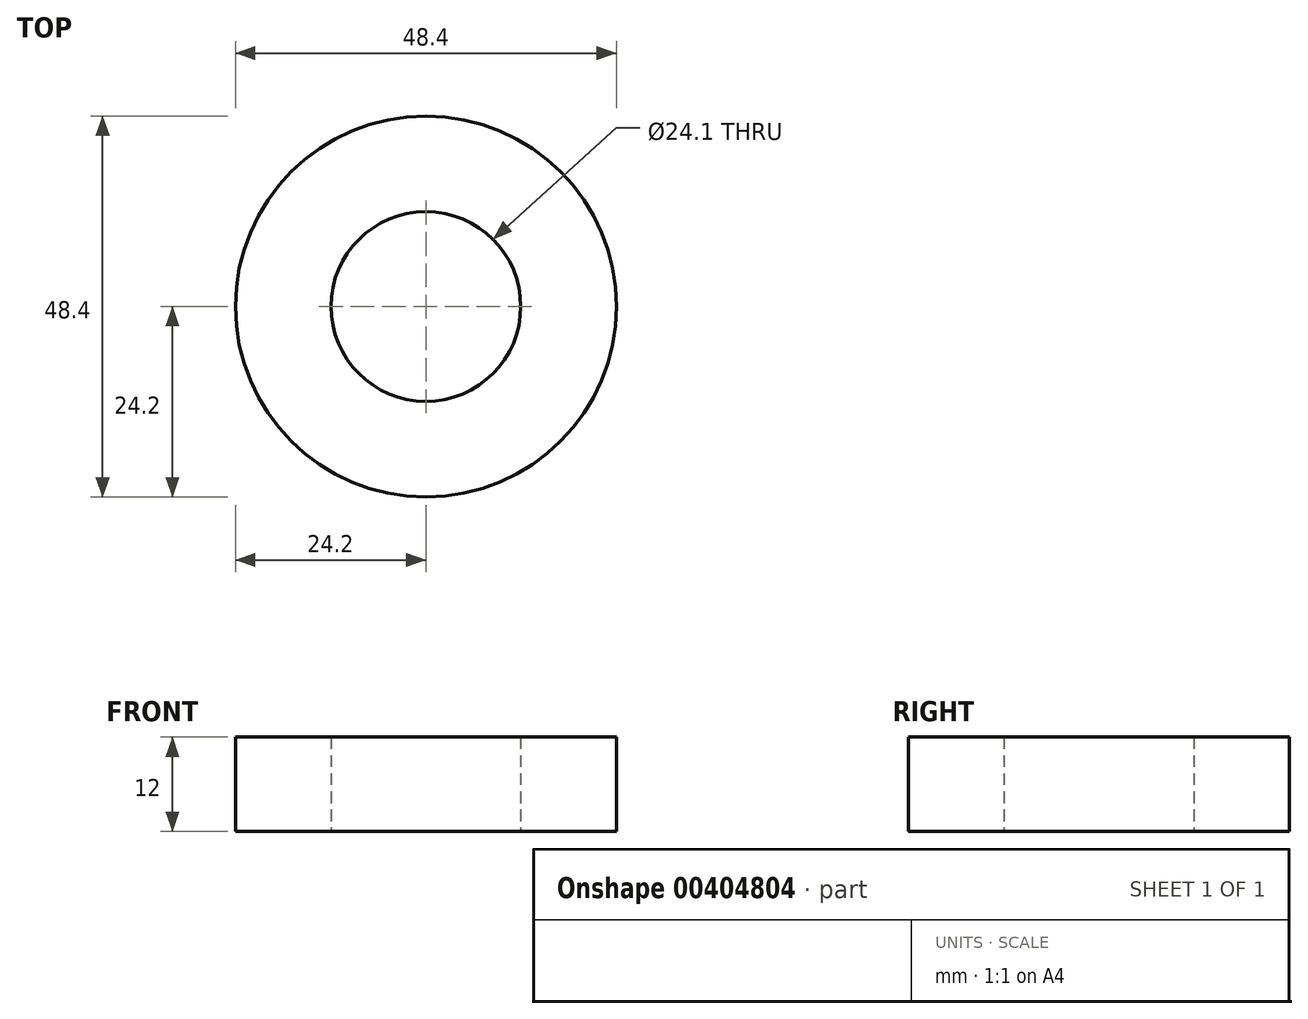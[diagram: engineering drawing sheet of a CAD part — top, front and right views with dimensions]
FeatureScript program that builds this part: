
annotation { "Feature Type Name" : "Feature", "Feature Type Description" : "" }
export const myFeature = defineFeature(function(context is Context, id is Id, definition is map)
    precondition{}
    {
        {
            var Q0;
            Q0=qCreatedBy(makeId("Top.planeOp"),FACE);
            var sketch = newSketch(context, id + "F0", { "sketchPlane" : qUnion([Q0])});
            skCircle(sketch, "E0", {"center": v(0, 0) * mm, "radius": 24.2 * mm});
            skCircle(sketch, "E1", {"center": v(0, 0) * mm, "radius": 12.05 * mm});
            skSolve(sketch);
        }
        {
            var Q0;
            Q0=makeQuery(id+"F0.imprint","IMPRINT",FACE,{"disambiguationData":[TD([[makeQuery(id+"F0.imprint","IMPRINT",EDGE,{"derivedFrom":sQuery(id+"F0.wireOp",EDGE,"E0")}),1.0]])]});
            extrude(context, id + "F1", {"entities" : qUnion([Q0]), "depth" : 12 * mm});
        }
    });
